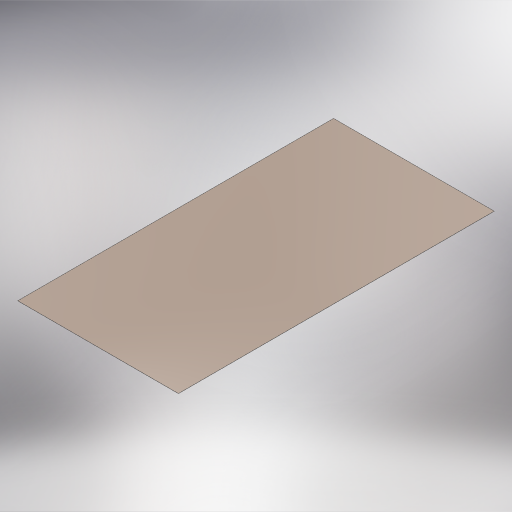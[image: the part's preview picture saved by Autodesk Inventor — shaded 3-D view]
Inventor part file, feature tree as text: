
AUTODESK INVENTOR PART (.ipt)
format: ipt  version: 2024 (Build 280153000, 153)  size: 294,912 bytes
history: native  units: in
note: dims shown in document units (in); Inventor stores cm internally (conversion verified against a paired STEP export)
features: extrude x1, sketch x1
ambient origin geometry x8: Origin, YZ Plane, XZ Plane, XY Plane, X Axis, Y Axis, Z Axis, Center Point
bodies: Solid1 (feature_tree)
feature tree (2):
  extrude  "Extrusion1"  Depth=2.2441in
  sketch  "Sketch1"  dims[d0=1.1417in d1=2.2441in d2=0.001in d3=0.0in]
